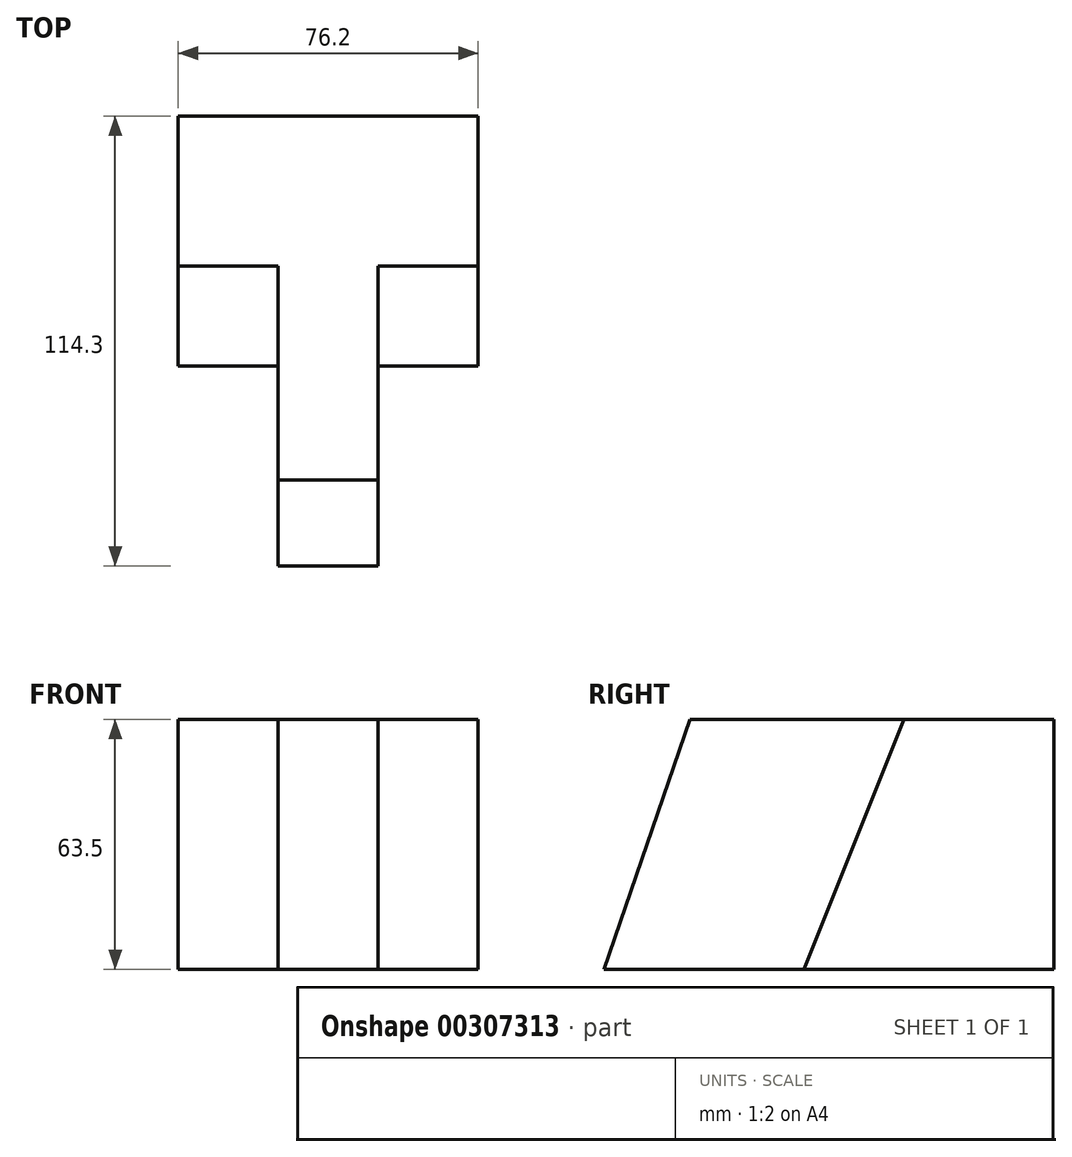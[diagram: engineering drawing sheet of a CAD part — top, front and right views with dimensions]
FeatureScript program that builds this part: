
annotation { "Feature Type Name" : "Feature", "Feature Type Description" : "" }
export const myFeature = defineFeature(function(context is Context, id is Id, definition is map)
    precondition{}
    {
        {
            var Q0;
            Q0=qCreatedBy(makeId("Top.planeOp"),FACE);
            var sketch = newSketch(context, id + "F0", { "sketchPlane" : qUnion([Q0])});
            skLineSegment(sketch, "E0", {"start": v(-97.22, 87.15) * mm, "end": v(-97.22, 23.65) * mm});
            skLineSegment(sketch, "E1", {"start": v(-97.22, 23.65) * mm, "end": v(-71.82, 23.65) * mm});
            skLineSegment(sketch, "E2", {"start": v(-71.82, 23.65) * mm, "end": v(-71.82, -27.15) * mm});
            skLineSegment(sketch, "E3", {"start": v(-71.82, -27.15) * mm, "end": v(-46.42, -27.15) * mm});
            skLineSegment(sketch, "E4", {"start": v(-46.42, -27.15) * mm, "end": v(-46.42, 23.65) * mm});
            skLineSegment(sketch, "E5", {"start": v(-46.42, 23.65) * mm, "end": v(-21.02, 23.65) * mm});
            skLineSegment(sketch, "E6", {"start": v(-21.02, 23.65) * mm, "end": v(-21.02, 87.15) * mm});
            skLineSegment(sketch, "E7", {"start": v(-21.02, 87.15) * mm, "end": v(-97.22, 87.15) * mm});
            skSolve(sketch);
        }
        {
            var Q0;
            Q0=makeQuery(id+"F0.imprint","IMPRINT",FACE,{"disambiguationData":[TD([[makeQuery(id+"F0.imprint","IMPRINT",EDGE,{"derivedFrom":sQuery(id+"F0.wireOp",EDGE,"E0")}),1.0]])]});
            extrude(context, id + "F1", {"entities" : qUnion([Q0]), "depth" : 63.5 * mm});
        }
        {
            var Q0;
            Q0=makeQuery(id+"F1.opExtrude","SWEPT_FACE",FACE,{"disambiguationData":[OSD([sQuery(id+"F0.wireOp",EDGE,"E0")])]});
            var sketch = newSketch(context, id + "F2", { "sketchPlane" : qUnion([Q0])});
            skLineSegment(sketch, "E8", {"start": v(-49.05, 63.5) * mm, "end": v(-23.65, 0) * mm});
            skLineSegment(sketch, "E9", {"start": v(-23.65, 0) * mm, "end": v(-23.65, 63.5) * mm});
            skLineSegment(sketch, "E10", {"start": v(-23.65, 63.5) * mm, "end": v(-49.05, 63.5) * mm});
            skLineSegment(sketch, "E11", {"start": v(-87.15, 63.5) * mm, "end": v(-49.05, 63.5) * mm});
            skLineSegment(sketch, "E12", {"start": v(-87.15, 0) * mm, "end": v(-23.65, 0) * mm});
            skSolve(sketch);
        }
        {
            var Q0;
            Q0=makeQuery(id+"F2.imprint","IMPRINT",FACE,{"disambiguationData":[TD([[makeQuery(id+"F2.imprint","IMPRINT",EDGE,{"derivedFrom":sQuery(id+"F2.wireOp",EDGE,"E8")}),1.0]])]});
            extrude(context, id + "F3", {"entities" : qUnion([Q0]), "operationType" : NewBodyOperationType.REMOVE, "oppositeDirection" : true, "depth" : 25.4 * mm});
        }
        {
            var Q0;
            Q0=makeQuery(id+"F1.opExtrude","SWEPT_FACE",FACE,{"disambiguationData":[OSD([sQuery(id+"F0.wireOp",EDGE,"E6")])]});
            var sketch = newSketch(context, id + "F4", { "sketchPlane" : qUnion([Q0])});
            skLineSegment(sketch, "E13", {"start": v(49.05, 63.5) * mm, "end": v(23.65, 0) * mm});
            skLineSegment(sketch, "E14", {"start": v(23.65, 0) * mm, "end": v(23.65, 63.5) * mm});
            skLineSegment(sketch, "E15", {"start": v(23.65, 63.5) * mm, "end": v(49.05, 63.5) * mm});
            skLineSegment(sketch, "E16", {"start": v(49.05, 63.5) * mm, "end": v(87.15, 63.5) * mm});
            skLineSegment(sketch, "E17", {"start": v(23.65, 0) * mm, "end": v(87.15, 0) * mm});
            skSolve(sketch);
        }
        {
            var Q0;
            Q0=makeQuery(id+"F4.imprint","IMPRINT",FACE,{"disambiguationData":[TD([[makeQuery(id+"F4.imprint","IMPRINT",EDGE,{"derivedFrom":sQuery(id+"F4.wireOp",EDGE,"E13")}),-1.0]])]});
            extrude(context, id + "F5", {"entities" : qUnion([Q0]), "operationType" : NewBodyOperationType.REMOVE, "oppositeDirection" : true, "depth" : 25.4 * mm});
        }
        {
            var Q0;
            Q0=makeQuery(id+"F5.boolean.opBoolean","MERGE",FACE,{"derivedFrom":[makeQuery(id+"F1.opExtrude","SWEPT_FACE",FACE,{"disambiguationData":[OSD([sQuery(id+"F0.wireOp",EDGE,"E4")])]}),makeQuery(id+"F5.opExtrude","CAP_FACE",FACE,{"disambiguationData":[OSD([sQuery(id+"F4.wireOp",EDGE,"E13"),sQuery(id+"F4.wireOp",EDGE,"E14"),sQuery(id+"F4.wireOp",EDGE,"E15")])],"isStart":false})]});
            var sketch = newSketch(context, id + "F6", { "sketchPlane" : qUnion([Q0])});
            skLineSegment(sketch, "E18", {"start": v(-5.36, 63.5) * mm, "end": v(-27.15, 0) * mm});
            skLineSegment(sketch, "E19", {"start": v(-27.15, 0) * mm, "end": v(-27.15, 63.5) * mm});
            skLineSegment(sketch, "E20", {"start": v(-27.15, 63.5) * mm, "end": v(-5.36, 63.5) * mm});
            skSolve(sketch);
        }
        {
            var Q0;
            Q0=makeQuery(id+"F6.imprint","IMPRINT",FACE,{"disambiguationData":[TD([[makeQuery(id+"F6.imprint","IMPRINT",EDGE,{"derivedFrom":sQuery(id+"F6.wireOp",EDGE,"E18")}),-1.0]])]});
            extrude(context, id + "F7", {"entities" : qUnion([Q0]), "operationType" : NewBodyOperationType.REMOVE, "endBound" : BoundingType.THROUGH_ALL, "oppositeDirection" : true, "depth" : 119.63 * mm});
        }
    });
